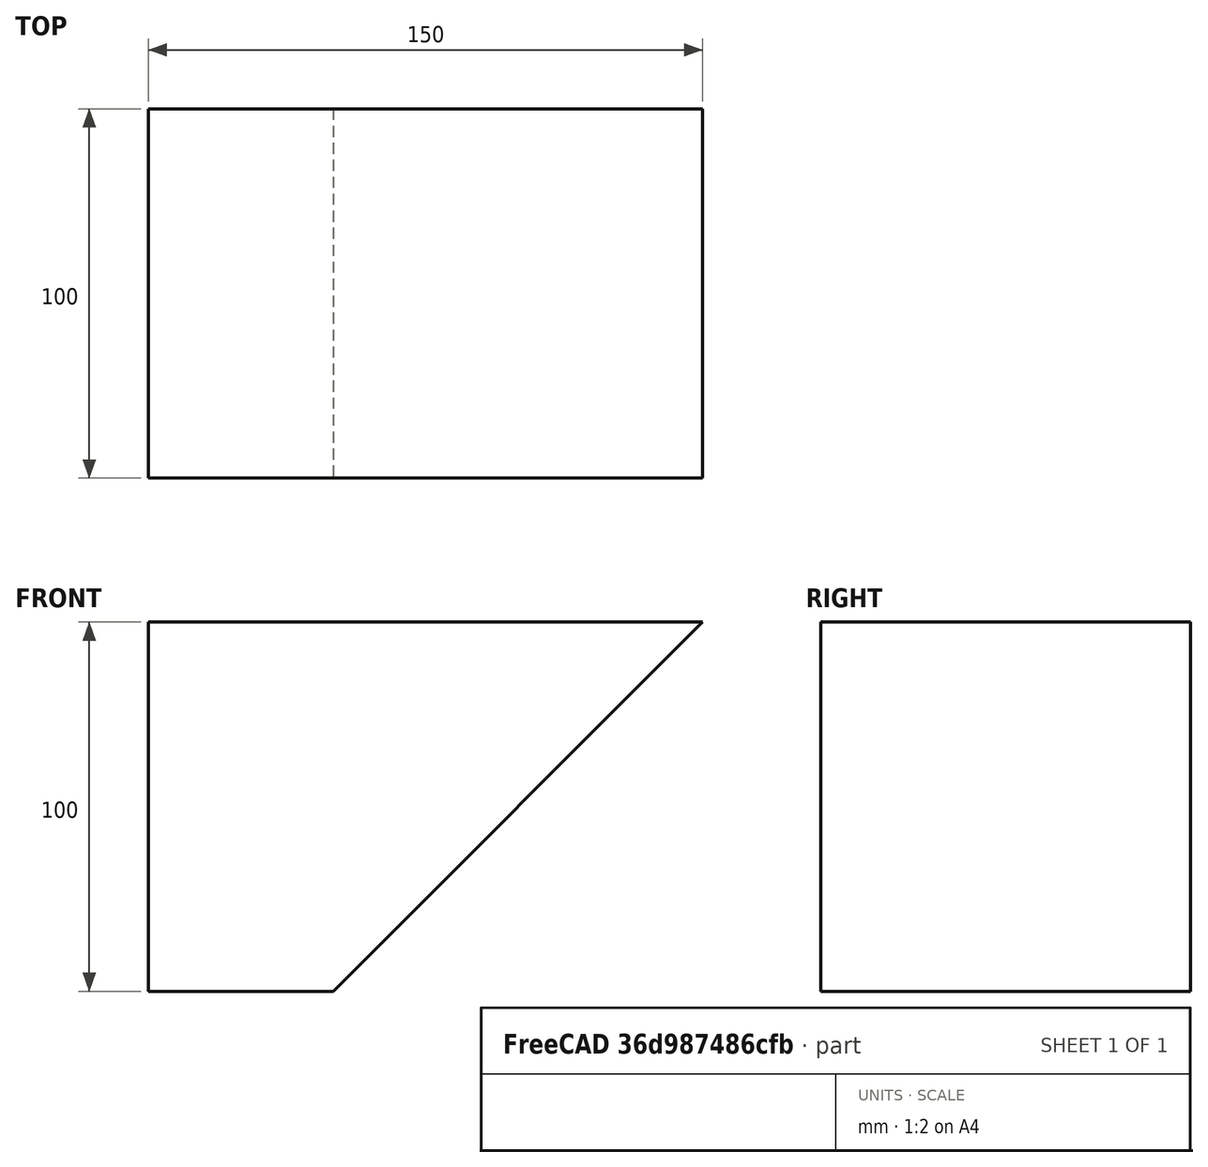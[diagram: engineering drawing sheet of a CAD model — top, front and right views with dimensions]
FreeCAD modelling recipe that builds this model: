
FCSTD DOCUMENT  (FreeCAD 0.16R6706 (Git))
Label: 45 degree rule
License: All rights reserved
LicenseURL: http://en.wikipedia.org/wiki/All_rights_reserved
objects: Drawing::FeatureViewPart×4, Sketcher::SketchObject×1, PartDesign::Pad×1, Drawing::FeaturePage×1
note: 3 computed .brp shape members not serialized (recipe doc carries the construction recipe); baked Part::Feature solids carry a one-line shape summary decoded from their .brp

FEATURE [Sketcher::SketchObject] Sketch
  Placement = pos=(0,0,0) rot=(-1,0,0;4.71239rad)
  sketch-geometry (4):
    g0: LineSegment StartX=0 StartY=100 StartZ=0 EndX=0 EndY=0 EndZ=0
    g1: LineSegment StartX=0 StartY=0 StartZ=0 EndX=50 EndY=0 EndZ=0
    g2: LineSegment StartX=50 StartY=0 StartZ=0 EndX=150 EndY=100 EndZ=0
    g3: LineSegment StartX=150 StartY=100 StartZ=0 EndX=0 EndY=100 EndZ=0
  constraints (12):
    c: PointOnObject(g0,g-1)
    c: Vertical(g0)
    c: Coincident(g0,g1)
    c: Horizontal(g1)
    c: Coincident(g1,g2)
    c: Coincident(g2,g3)
    c: Horizontal(g3)
    c: Coincident(g0,g3)
    c: Tangent(g0,g-2) = 1.5708
    c: DistanceX(g1,g1) = 50
    c: DistanceY(g0,g0) = 100
    c: Angle(g2,g-1) = 2.35619
FEATURE [PartDesign::Pad] Pad
  Length = 100
  Length2 = 100
  Placement = pos=(0,0,0) rot=(-1,0,0;4.71239rad)
  Sketch = -> Sketch
  Type = 0
FEATURE [Drawing::FeatureViewPart] Ortho  label="Ortho_0_0"
  Direction = (1,0,0)
  HiddenWidth = 0.15
  LineWidth = 0.35
  Rotation = -90
  Scale = 0.375
  ShowHiddenLines = false
  ShowSmoothLines = false
  Source = -> Pad
  Tolerance = 0.05
  ViewResult = <g id="Ortho_0_0"\n   transform="rotate(-90,123.75,229.25) translate(123.75,229.25) scale(0.375,0.375)"\n  >\n<g   stroke="rgb(0, 0, 0)"\n   stroke-width="0.933333"\n   stroke-linecap="butt"\n   stroke-linejoin="miter"\n   fill="none"\n   transform="scale(1,-1)"\n  >\n<path id= "1" d=" M 0 0 L 4.44089e-14 100 " />\n<path id= "2" d=" M 100 -6.66134e-14 L 100 100 " />\n<path id= "3" d=" M 0 0 L 100 -6.66134e-14 " />\n<path id= "4" d=" M 4.44089e-14 100 L 100 100 " />\n</g>\n</g>
  Visible = true
  X = 123.75
  Y = 229.25
FEATURE [Drawing::FeatureViewPart] Ortho001  label="Ortho_0_1"
  Direction = (0,0,1)
  HiddenWidth = 0.15
  LineWidth = 0.35
  Rotation = 90
  Scale = 0.375
  ShowHiddenLines = false
  ShowSmoothLines = false
  Source = -> Pad
  Tolerance = 0.05
  ViewResult = <g id="Ortho_0_1"\n   transform="rotate(90,123.75,67.75) translate(123.75,67.75) scale(0.375,0.375)"\n  >\n<g   stroke="rgb(0, 0, 0)"\n   stroke-width="0.933333"\n   stroke-linecap="butt"\n   stroke-linejoin="miter"\n   fill="none"\n   transform="scale(1,-1)"\n  >\n<path id= "1" d=" M 0 6.66134e-14 L 0 -100 " />\n<path id= "2" d=" M 150 6.66134e-14 L 150 -100 " />\n<path id= "3" d=" M 150 6.66134e-14 L -2.84217e-14 6.66134e-14 " />\n<path id= "4" d=" M 150 -100 L -2.84217e-14 -100 " />\n</g>\n</g>
  Visible = true
  X = 123.75
  Y = 67.75
FEATURE [Drawing::FeatureViewPart] Ortho002  label="Ortho_1_0"
  Direction = (0,1,0)
  HiddenWidth = 0.15
  LineWidth = 0.35
  Rotation = -90
  Scale = 0.375
  ShowHiddenLines = false
  ShowSmoothLines = false
  Source = -> Pad
  Tolerance = 0.05
  ViewResult = <g id="Ortho_1_0"\n   transform="rotate(-90,195,229.25) translate(195,229.25) scale(0.375,0.375)"\n  >\n<g   stroke="rgb(0, 0, 0)"\n   stroke-width="0.933333"\n   stroke-linecap="butt"\n   stroke-linejoin="miter"\n   fill="none"\n   transform="scale(1,-1)"\n  >\n<path id= "1" d=" M 100 0 L -2.84217e-14 0 " />\n<path id= "2" d=" M 0 0 L 0 50 " />\n<path id= "3" d=" M 0 50 L 100 150 " />\n<path id= "4" d=" M 100 150 L 100 -2.84217e-14 " />\n</g>\n</g>
  Visible = true
  X = 195
  Y = 229.25
FEATURE [Drawing::FeatureViewPart] Ortho003  label="Ortho_-1_0"
  Direction = (0,-1,0)
  HiddenWidth = 0.15
  LineWidth = 0.35
  Rotation = 90
  Scale = 0.375
  ShowHiddenLines = false
  ShowSmoothLines = false
  Source = -> Pad
  Tolerance = 0.05
  ViewResult = <g id="Ortho_-1_0"\n   transform="rotate(90,15,229.25) translate(15,229.25) scale(0.375,0.375)"\n  >\n<g   stroke="rgb(0, 0, 0)"\n   stroke-width="0.933333"\n   stroke-linecap="butt"\n   stroke-linejoin="miter"\n   fill="none"\n   transform="scale(1,-1)"\n  >\n<path id= "1" d=" M -100 0 L -1.42109e-14 0 " />\n<path id= "2" d=" M -4.44089e-14 0 L -4.44089e-14 50 " />\n<path id= "3" d=" M -4.44089e-14 50 L -100 150 " />\n<path id= "4" d=" M -100 150 L -100 -2.84217e-14 " />\n</g>\n</g>
  Visible = true
  X = 15
  Y = 229.25
FEATURE [Drawing::FeaturePage] Page
  Group = -> [Ortho,Ortho001,Ortho002,Ortho003]
